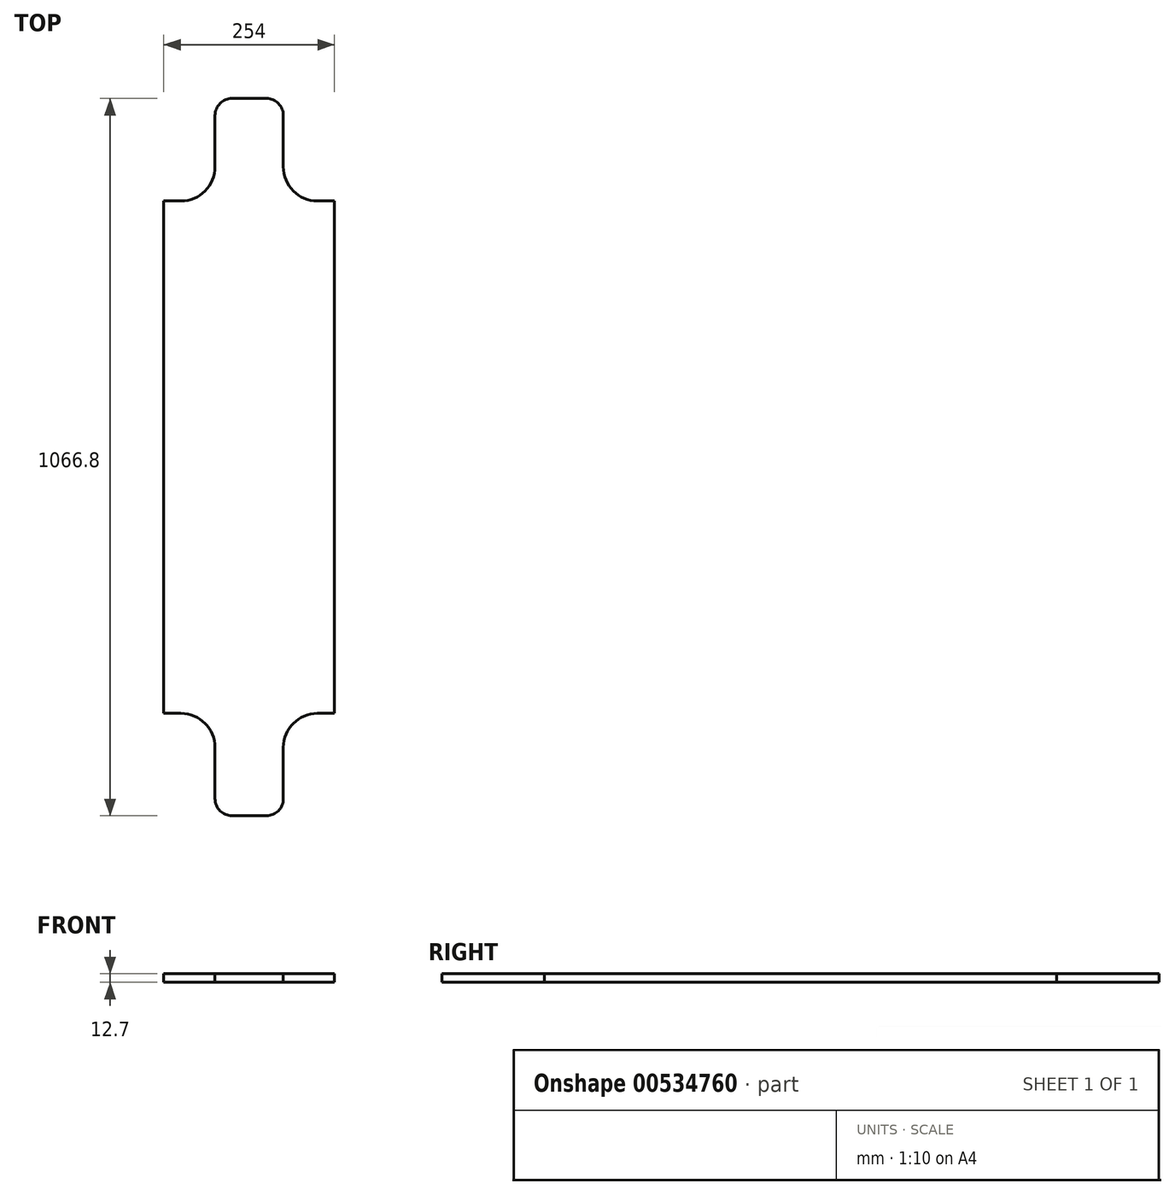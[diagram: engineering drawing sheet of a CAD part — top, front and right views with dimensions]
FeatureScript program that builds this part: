
annotation { "Feature Type Name" : "Feature", "Feature Type Description" : "" }
export const myFeature = defineFeature(function(context is Context, id is Id, definition is map)
    precondition{}
    {
        {
            var Q0;
            Q0=qCreatedBy(makeId("Top.planeOp"),FACE);
            var sketch = newSketch(context, id + "F0", { "sketchPlane" : qUnion([Q0])});
            skLineSegment(sketch, "E0.bottom", {"start": v(-127, 381) * mm, "end": v(-50.8, 381) * mm});
            skLineSegment(sketch, "E0.top", {"start": v(-127, 0) * mm, "end": v(127, 0) * mm, "construction": true});
            skLineSegment(sketch, "E0.left", {"start": v(-127, 381) * mm, "end": v(-127, 0) * mm});
            skLineSegment(sketch, "E0.right", {"start": v(127, 381) * mm, "end": v(127, 0) * mm});
            skLineSegment(sketch, "E1.top", {"start": v(-50.8, 533.4) * mm, "end": v(50.8, 533.4) * mm});
            skLineSegment(sketch, "E1.left", {"start": v(-50.8, 381) * mm, "end": v(-50.8, 533.4) * mm});
            skLineSegment(sketch, "E1.right", {"start": v(50.8, 381) * mm, "end": v(50.8, 533.4) * mm});
            skLineSegment(sketch, "E2.trimOffspring", {"start": v(50.8, 381) * mm, "end": v(127, 381) * mm});
            skLineSegment(sketch, "E3", {"start": v(0, 533.4) * mm, "end": v(0, 0) * mm, "construction": true});
            skLineSegment(sketch, "E4.MirrorCS", {"start": v(127, -381) * mm, "end": v(127, 0) * mm});
            skLineSegment(sketch, "E5.MirrorCS", {"start": v(50.8, -381) * mm, "end": v(127, -381) * mm});
            skLineSegment(sketch, "E6.MirrorCS", {"start": v(50.8, -381) * mm, "end": v(50.8, -533.4) * mm});
            skLineSegment(sketch, "E7.MirrorCS", {"start": v(-50.8, -533.4) * mm, "end": v(50.8, -533.4) * mm});
            skLineSegment(sketch, "E8.MirrorCS", {"start": v(-50.8, -381) * mm, "end": v(-50.8, -533.4) * mm});
            skLineSegment(sketch, "E9.MirrorCS", {"start": v(-127, -381) * mm, "end": v(-127, 0) * mm});
            skLineSegment(sketch, "E10.MirrorCS", {"start": v(-127, -381) * mm, "end": v(-50.8, -381) * mm});
            skSolve(sketch);
        }
        {
            var Q0;
            Q0 = qSketchRegion(id + "F0", true);
            extrude(context, id + "F1", {"entities" : qUnion([Q0]), "depth" : 12.7 * mm, "offsetDistance" : 25.4 * mm});
        }
        {
            var Q0;
            Q0=makeQuery(id+"F1.opExtrude","SWEPT_EDGE",EDGE,{"disambiguationData":[OSD([sQuery(id+"F0.wireOp",EDGE,"E0.bottom"),sQuery(id+"F0.wireOp",EDGE,"E1.left")])]});
            var Q1;
            Q1=makeQuery(id+"F1.opExtrude","SWEPT_EDGE",EDGE,{"disambiguationData":[OSD([sQuery(id+"F0.wireOp",EDGE,"E1.right"),sQuery(id+"F0.wireOp",EDGE,"E2.trimOffspring")])]});
            var Q2;
            Q2=makeQuery(id+"F1.opExtrude","SWEPT_EDGE",EDGE,{"disambiguationData":[OSD([sQuery(id+"F0.wireOp",EDGE,"E8.MirrorCS"),sQuery(id+"F0.wireOp",EDGE,"E10.MirrorCS")])]});
            var Q3;
            Q3=makeQuery(id+"F1.opExtrude","SWEPT_EDGE",EDGE,{"disambiguationData":[OSD([sQuery(id+"F0.wireOp",EDGE,"E5.MirrorCS"),sQuery(id+"F0.wireOp",EDGE,"E6.MirrorCS")])]});
            fillet(context, id + "F2", {"entities" : qUnion([Q0, Q1, Q2, Q3]), "radius" : 50.8 * mm, "tangentPropagation" : true, "allowEdgeOverflow" : false});
        }
        {
            var Q0;
            Q0=makeQuery(id+"F1.opExtrude","SWEPT_EDGE",EDGE,{"disambiguationData":[OSD([sQuery(id+"F0.wireOp",EDGE,"E7.MirrorCS"),sQuery(id+"F0.wireOp",EDGE,"E8.MirrorCS")])]});
            var Q1;
            Q1=makeQuery(id+"F1.opExtrude","SWEPT_EDGE",EDGE,{"disambiguationData":[OSD([sQuery(id+"F0.wireOp",EDGE,"E6.MirrorCS"),sQuery(id+"F0.wireOp",EDGE,"E7.MirrorCS")])]});
            var Q2;
            Q2=makeQuery(id+"F1.opExtrude","SWEPT_EDGE",EDGE,{"disambiguationData":[OSD([sQuery(id+"F0.wireOp",EDGE,"E1.top"),sQuery(id+"F0.wireOp",EDGE,"E1.right")])]});
            var Q3;
            Q3=makeQuery(id+"F1.opExtrude","SWEPT_EDGE",EDGE,{"disambiguationData":[OSD([sQuery(id+"F0.wireOp",EDGE,"E1.top"),sQuery(id+"F0.wireOp",EDGE,"E1.left")])]});
            fillet(context, id + "F3", {"entities" : qUnion([Q0, Q1, Q2, Q3]), "radius" : 25.4 * mm, "tangentPropagation" : true, "allowEdgeOverflow" : false});
        }
    });
